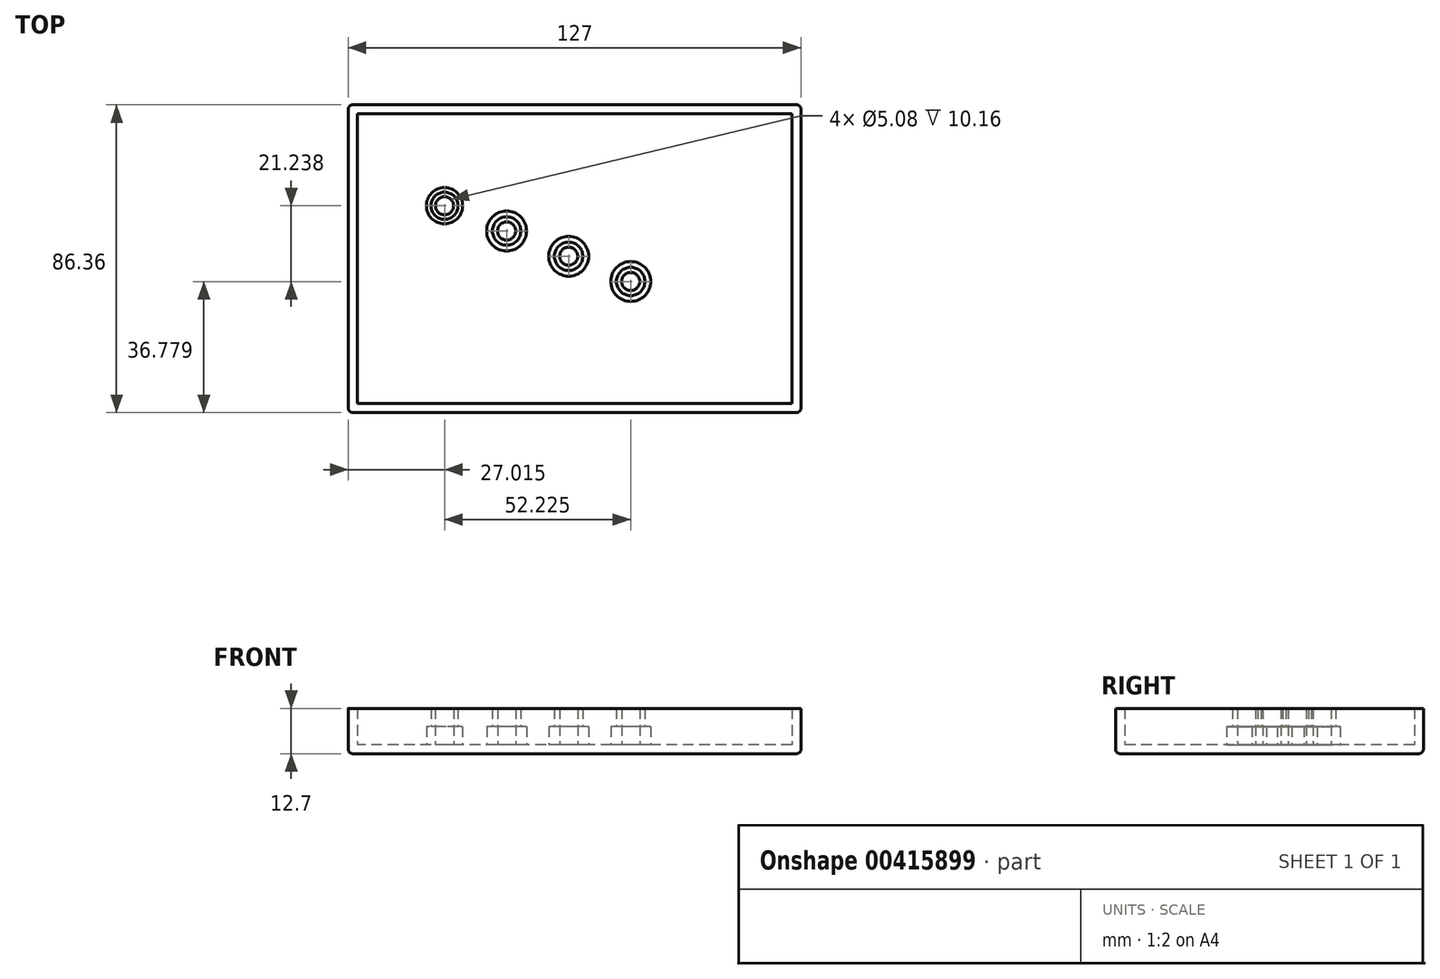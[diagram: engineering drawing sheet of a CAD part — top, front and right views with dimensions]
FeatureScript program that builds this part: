
annotation { "Feature Type Name" : "Feature", "Feature Type Description" : "" }
export const myFeature = defineFeature(function(context is Context, id is Id, definition is map)
    precondition{}
    {
        {
            var Q0;
            Q0=qCreatedBy(makeId("Top.planeOp"),FACE);
            var sketch = newSketch(context, id + "F0", { "sketchPlane" : qUnion([Q0])});
            skLineSegment(sketch, "E0.bottom", {"start": v(63.5, 43.18) * mm, "end": v(-63.5, 43.18) * mm});
            skLineSegment(sketch, "E0.top", {"start": v(63.5, -43.18) * mm, "end": v(-63.5, -43.18) * mm});
            skLineSegment(sketch, "E0.left", {"start": v(63.5, 43.18) * mm, "end": v(63.5, -43.18) * mm});
            skLineSegment(sketch, "E0.right", {"start": v(-63.5, 43.18) * mm, "end": v(-63.5, -43.18) * mm});
            skPoint(sketch, "E0.middle", {"position": v(0, 0) * mm});
            skSolve(sketch);
        }
        {
            var Q0;
            Q0=makeQuery(id+"F0.imprint","IMPRINT",FACE,{"disambiguationData":[TD([[makeQuery(id+"F0.imprint","IMPRINT",EDGE,{"derivedFrom":sQuery(id+"F0.wireOp",EDGE,"E0.bottom")}),1.0]])]});
            extrude(context, id + "F1", {"entities" : qUnion([Q0]), "depth" : 12.7 * mm});
        }
        {
            var Q0;
            Q0=makeQuery(id+"F1.opExtrude","CAP_FACE",FACE,{"disambiguationData":[OSD([sQuery(id+"F0.wireOp",EDGE,"E0.bottom"),sQuery(id+"F0.wireOp",EDGE,"E0.top"),sQuery(id+"F0.wireOp",EDGE,"E0.left"),sQuery(id+"F0.wireOp",EDGE,"E0.right")])],"isStart":false});
            shell(context, id + "F2", {"entities" : qUnion([Q0]), "thickness" : 2.54 * mm});
        }
        {
            var Q0;
            Q0=makeQuery(id+"F1.opExtrude","SWEPT_EDGE",EDGE,{"disambiguationData":[OSD([sQuery(id+"F0.wireOp",EDGE,"E0.bottom"),sQuery(id+"F0.wireOp",EDGE,"E0.right")])]});
            var Q1;
            Q1=makeQuery(id+"F1.opExtrude","CAP_EDGE",EDGE,{"disambiguationData":[OSD([sQuery(id+"F0.wireOp",EDGE,"E0.right")])],"isStart":true});
            var Q2;
            Q2=makeQuery(id+"F1.opExtrude","CAP_EDGE",EDGE,{"disambiguationData":[OSD([sQuery(id+"F0.wireOp",EDGE,"E0.top")])],"isStart":true});
            var Q3;
            Q3=makeQuery(id+"F1.opExtrude","CAP_EDGE",EDGE,{"disambiguationData":[OSD([sQuery(id+"F0.wireOp",EDGE,"E0.bottom")])],"isStart":true});
            var Q4;
            Q4=makeQuery(id+"F1.opExtrude","CAP_EDGE",EDGE,{"disambiguationData":[OSD([sQuery(id+"F0.wireOp",EDGE,"E0.left")])],"isStart":true});
            var Q5;
            Q5=makeQuery(id+"F1.opExtrude","SWEPT_EDGE",EDGE,{"disambiguationData":[OSD([sQuery(id+"F0.wireOp",EDGE,"E0.bottom"),sQuery(id+"F0.wireOp",EDGE,"E0.left")])]});
            var Q6;
            Q6=makeQuery(id+"F1.opExtrude","SWEPT_EDGE",EDGE,{"disambiguationData":[OSD([sQuery(id+"F0.wireOp",EDGE,"E0.top"),sQuery(id+"F0.wireOp",EDGE,"E0.left")])]});
            var Q7;
            Q7=makeQuery(id+"F1.opExtrude","SWEPT_EDGE",EDGE,{"disambiguationData":[OSD([sQuery(id+"F0.wireOp",EDGE,"E0.top"),sQuery(id+"F0.wireOp",EDGE,"E0.right")])]});
            fillet(context, id + "F3", {"entities" : qUnion([Q0, Q1, Q2, Q3, Q4, Q5, Q6, Q7]), "radius" : 1.27 * mm, "tangentPropagation" : true, "allowEdgeOverflow" : false});
        }
        {
            var Q0;
            Q0=makeQuery(id+"F2.opShell","OFFSET_FACE",FACE,{"disambiguationData":[OSD([sQuery(id+"F0.wireOp",EDGE,"E0.bottom"),sQuery(id+"F0.wireOp",EDGE,"E0.top"),sQuery(id+"F0.wireOp",EDGE,"E0.left"),sQuery(id+"F0.wireOp",EDGE,"E0.right")])]});
            var sketch = newSketch(context, id + "F4", { "sketchPlane" : qUnion([Q0])});
            skCircle(sketch, "E1", {"center": v(-36.49, 14.84) * mm, "radius": 2.54 * mm});
            skCircle(sketch, "E2", {"center": v(-36.49, 14.84) * mm, "radius": 3.81 * mm});
            skCircle(sketch, "E3", {"center": v(-36.49, 14.84) * mm, "radius": 5.08 * mm});
            skCircle(sketch, "E4", {"center": v(-1.67, 0.68) * mm, "radius": 2.54 * mm});
            skCircle(sketch, "E5", {"center": v(-1.67, 0.68) * mm, "radius": 3.99 * mm});
            skCircle(sketch, "E6", {"center": v(-1.67, 0.68) * mm, "radius": 5.6 * mm});
            skCircle(sketch, "E7", {"center": v(-19.08, 7.76) * mm, "radius": 2.54 * mm});
            skCircle(sketch, "E8", {"center": v(-19.08, 7.76) * mm, "radius": 3.99 * mm});
            skCircle(sketch, "E9", {"center": v(-19.08, 7.76) * mm, "radius": 5.6 * mm});
            skCircle(sketch, "E10", {"center": v(15.74, -6.4) * mm, "radius": 2.54 * mm});
            skCircle(sketch, "E11", {"center": v(15.74, -6.4) * mm, "radius": 3.99 * mm});
            skCircle(sketch, "E12", {"center": v(15.74, -6.4) * mm, "radius": 5.6 * mm});
            skSolve(sketch);
        }
        {
            var Q0;
            Q0=makeQuery(id+"F4.imprint","IMPRINT",FACE,{"disambiguationData":[TD([[makeQuery(id+"F4.imprint","IMPRINT",EDGE,{"derivedFrom":sQuery(id+"F4.wireOp",EDGE,"E1")}),-1.0]])]});
            var Q1;
            Q1=makeQuery(id+"F4.imprint","IMPRINT",FACE,{"disambiguationData":[TD([[makeQuery(id+"F4.imprint","IMPRINT",EDGE,{"derivedFrom":sQuery(id+"F4.wireOp",EDGE,"E4")}),-1.0]])]});
            extrude(context, id + "F5", {"entities" : qUnion([Q0, Q1]), "operationType" : NewBodyOperationType.ADD, "depth" : 10.16 * mm});
        }
        {
            var Q0;
            Q0=makeQuery(id+"F4.imprint","IMPRINT",FACE,{"disambiguationData":[TD([[makeQuery(id+"F4.imprint","IMPRINT",EDGE,{"derivedFrom":sQuery(id+"F4.wireOp",EDGE,"E2")}),-1.0]])]});
            var Q1;
            Q1=makeQuery(id+"F4.imprint","IMPRINT",FACE,{"disambiguationData":[TD([[makeQuery(id+"F4.imprint","IMPRINT",EDGE,{"derivedFrom":sQuery(id+"F4.wireOp",EDGE,"E5")}),-1.0]])]});
            extrude(context, id + "F6", {"entities" : qUnion([Q0, Q1]), "operationType" : NewBodyOperationType.ADD, "depth" : 5.08 * mm});
        }
        {
            var Q0;
            Q0=makeQuery(id+"F4.imprint","IMPRINT",FACE,{"disambiguationData":[TD([[makeQuery(id+"F4.imprint","IMPRINT",EDGE,{"derivedFrom":sQuery(id+"F4.wireOp",EDGE,"E7")}),-1.0]])]});
            var Q1;
            Q1=makeQuery(id+"F4.imprint","IMPRINT",FACE,{"disambiguationData":[TD([[makeQuery(id+"F4.imprint","IMPRINT",EDGE,{"derivedFrom":sQuery(id+"F4.wireOp",EDGE,"E10")}),-1.0]])]});
            extrude(context, id + "F7", {"entities" : qUnion([Q0, Q1]), "operationType" : NewBodyOperationType.ADD, "depth" : 10.16 * mm});
        }
        {
            var Q0;
            Q0=makeQuery(id+"F4.imprint","IMPRINT",FACE,{"disambiguationData":[TD([[makeQuery(id+"F4.imprint","IMPRINT",EDGE,{"derivedFrom":sQuery(id+"F4.wireOp",EDGE,"E8")}),-1.0]])]});
            var Q1;
            Q1=makeQuery(id+"F4.imprint","IMPRINT",FACE,{"disambiguationData":[TD([[makeQuery(id+"F4.imprint","IMPRINT",EDGE,{"derivedFrom":sQuery(id+"F4.wireOp",EDGE,"E11")}),-1.0]])]});
            extrude(context, id + "F8", {"entities" : qUnion([Q0, Q1]), "operationType" : NewBodyOperationType.ADD, "depth" : 5.08 * mm});
        }
    });
